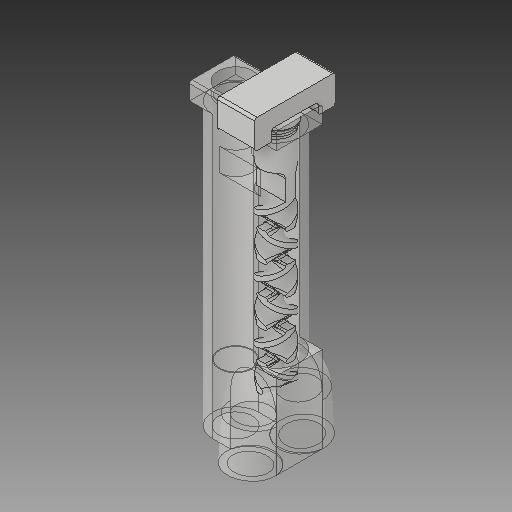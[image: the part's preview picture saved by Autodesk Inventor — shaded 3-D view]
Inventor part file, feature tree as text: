
AUTODESK INVENTOR PART (.ipt)
format: ipt  version: 2018 (Build 220112000, 112)  size: 1,804,800 bytes
history: native  units: mm
features: extrude x22, sketch x20, projected_geometry x7, fillet x6, other x6, sweep x5, pattern_linear x3, plane x2, boolean_combine x2, thicken_offset x2, mirror x1
ambient origin geometry x8: Origin, YZ Plane, XZ Plane, XY Plane, X Axis, Y Axis, Z Axis, Center Point
bodies: Solid10 (feature_tree), Solid11 (feature_tree)
feature tree (76):
  sketch  "Sketch24"  dims[d80=0.5mm]
  sketch  "Sketch18"  dims[d53=4.0mm d65=10.5mm]
  sketch  "Sketch22"  dims[d66=0.0mm d67=180.0deg d74=5.5mm]
  plane  "Work Plane3"
  sketch  "Sketch23"  dims[d78=5.5mm d79=1.8mm]
  sweep  "Sweep11"
  extrude  "Extrusion4"  Depth=5.5mm
  extrude  "Extrusion5"  Depth=1.8mm
  pattern_linear  "Rectangular Pattern4"  Spacing1=0.0mm  [1 undecoded]
  plane  "Work Plane4"
  extrude  "Extrusion6"  Depth=0.05mm
  sweep  "Sweep12"
  extrude  "Extrusion7"  Depth=0.05mm
  pattern_linear  "Rectangular Pattern8"  Count1=2  [1 undecoded]
  boolean_combine  "Combine1"
  fillet  "Fillet7"  Radius=8.0mm
  fillet  "Fillet8"  Radius=7.1mm
  pattern_linear  "Rectangular Pattern3"  Spacing1=37.0mm  [1 undecoded]
  boolean_combine  "Combine2"
  fillet  "Fillet9"  [1 undecoded]
  extrude  "Extrusion8"  Depth=4.0mm
  extrude  "Extrusion9"  Depth=7.1mm
  extrude  "Extrusion10"  TaperAngle=0.0deg  [1 undecoded]
  extrude  "Extrusion11"  Depth=0.05mm TaperAngle=0.0deg
  sketch  "Sketch33"  dims[d90=0.5mm]
  sketch  "Sketch34"  dims[d91=0.0mm]
  sketch  "Sketch49"  dims[d94=0.0mm]
  extrude  "tolerance"  Depth=4.0mm TaperAngle=0.0deg
  extrude  "tolerance_down"  Depth=0.05mm
  extrude  "Extrusion36"  Depth=3.0mm TaperAngle=0.0deg
  fillet  "Fillet24"  Radius=3.0mm
  extrude  "Extrusion12"  Depth=3.0mm
  extrude  "Extrusion13"  Depth=3.0mm TaperAngle=0.0deg
  extrude  "Extrusion14"  Depth=2.0mm TaperAngle=0.0deg
  fillet  "Fillet11"  Radius=1.0mm
  sketch  "Sketch46"  dims[d92=4.5mm]
  extrude  "Extrusion25"  Depth=10.0mm TaperAngle=0.0deg
  sketch  "Sketch47"  dims[d93=0.5mm]
  extrude  "down block"  Depth=8.0mm
  sketch  "Sketch57_not_used"  dims[d98=0.5mm d99=0.0mm d100=0.25mm d101=20.0mm d103=10.0mm d104=0.25mm d105=20.0mm d107=20.0mm d109=8.0mm d110=7.1mm d111=37.0mm d112=0.0mm d113=4.0mm d114=7.1mm d115=0.0mm d116=15.0mm d117=0.0mm d119=1.25mm d120=4.0mm d121=0.0mm d122=5.5mm d123=3.0mm d124=0.0mm d125=3.0mm d126=0.0mm d127=3.0mm d128=3.0mm d129=0.0mm d130=2.0mm d131=0.0mm d133=1.0mm d188=10.0mm d189=0.0mm d190=8.0mm d191=5.8mm d192=15.0mm d193=0.0mm d194=10.0mm d195=0.0mm d200=5.5mm d205=5.5mm d206=0.08mm d207=34.2mm d208=0.0mm d209=5.0mm d210=0.0mm d220=2.0mm d226=60.0deg d227=8.0mm d228=3.0mm d235=0.35mm d238=8.0mm d239=0.0mm d240=0.0mm d241=4.0mm d242=0.0mm d243=0.0mm d245=5.8mm d246=10.0mm d247=0.0mm d250=4.5mm d251=0.4mm d252=0.5mm d253=0.5mm d257=11.0mm d258=7.29726mm d259=16.407113mm d260=20.0mm d262=10.0mm d263=10.0mm d264=0.0mm d265=5.0mm d266=0.0mm d267=11.0mm d268=0.5mm d269=0.3mm d270=7.351222mm d271=1.9mm d272=0.0mm d275=2.0mm d276=0.1mm d279=0.1mm d280=2.0mm d281=0.0mm d282=0.05mm d283=0.05mm d284=0.05mm d285=0.05mm]
  extrude  "Extrusion27"  Depth=0.05mm
  sketch  "Sketch53"  dims[d95=4.0mm]
  sweep  "Sweep18"
  sweep  "Sweep19"
  mirror  "Mirror5"
  extrude  "Extrusion32"  Depth=0.05mm
  fillet  "Fillet23"  Radius=5.5mm
  extrude  "Extrusion35"  Depth=0.05mm
  extrude  "Extrusion38"  Depth=0.05mm TaperAngle=0.0deg
  thicken_offset  "Thicken3"
  thicken_offset  "Thicken4"
  other  "Srf2"
  other  "Srf4"
  other  "Srf5"
  other  "mixer_core"
  sketch  "Sketch25"  dims[d81=0.0mm]
  projected_geometry  "Projected Loop2"
  sketch  "Sketch26"  dims[d82=0.5mm]
  sketch  "Sketch27"  dims[d83=0.0mm]
  projected_geometry  "Projected Loop3"
  sketch  "Sketch28"  dims[d84=1.8mm]
  sketch  "Sketch29"  dims[d85=0.0mm d86=180.0deg]
  projected_geometry  "Projected Loop4"
  other  "mixer_cover"
  sketch  "Sketch30"  dims[d87=0.5mm]
  sketch  "Sketch31"  dims[d88=0.0mm]
  projected_geometry  "Projected Loop5"
  sketch  "Sketch32"  dims[d89=0.5mm]
  projected_geometry  "Projected Loop6"
  projected_geometry  "Projected Loop7"
  projected_geometry  "Projected Loop11"
  sketch  "Sketch55"  dims[d96=0.0mm d97=-31.415927mm]
  other  "Pattern of Solid10:2"
  sweep  "SweepSrf2"
  extrude  "ExtrusionSrf1"  Depth=2.0mm
  extrude  "ExtrusionSrf2"  TaperAngle=60.0deg  [1 undecoded]
note: 6 required parameter values undecoded (feature->parameter linkage not recoverable at this tier; creation-order binding heuristic only, values carry confidence <= 0.55)
